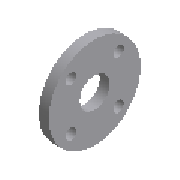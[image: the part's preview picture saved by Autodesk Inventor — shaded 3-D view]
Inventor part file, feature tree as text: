
AUTODESK INVENTOR PART (.ipt)
format: ipt  version: 2024.2 (Build 282272000, 272)  size: 170,496 bytes
history: native  units: mm (DEFAULTED — no unit token found)
features: other x5, revolve x1, extrude x1, pattern_circular x1
ambient origin geometry x8: Origin, YZ Plane, XZ Plane, XY Plane, X Axis, Y Axis, Z Axis, Center Point
bodies: Solid1 (feature_tree)
feature tree (8):
  revolve  "Revolution1"  Angle=90.0deg
  extrude  "Extrusion1"  Depth=300.0mm
  pattern_circular  "Circular Pattern1"  Count=3  [1 undecoded]
  other  "Work Axis1"
  other  "Work Point1"
  other  "Work Axis2"
  other  "Work Point2"
  other  "Work Point3"
note: 1 required parameter value undecoded (feature->parameter linkage not recoverable at this tier; creation-order binding heuristic only, values carry confidence <= 0.55)
